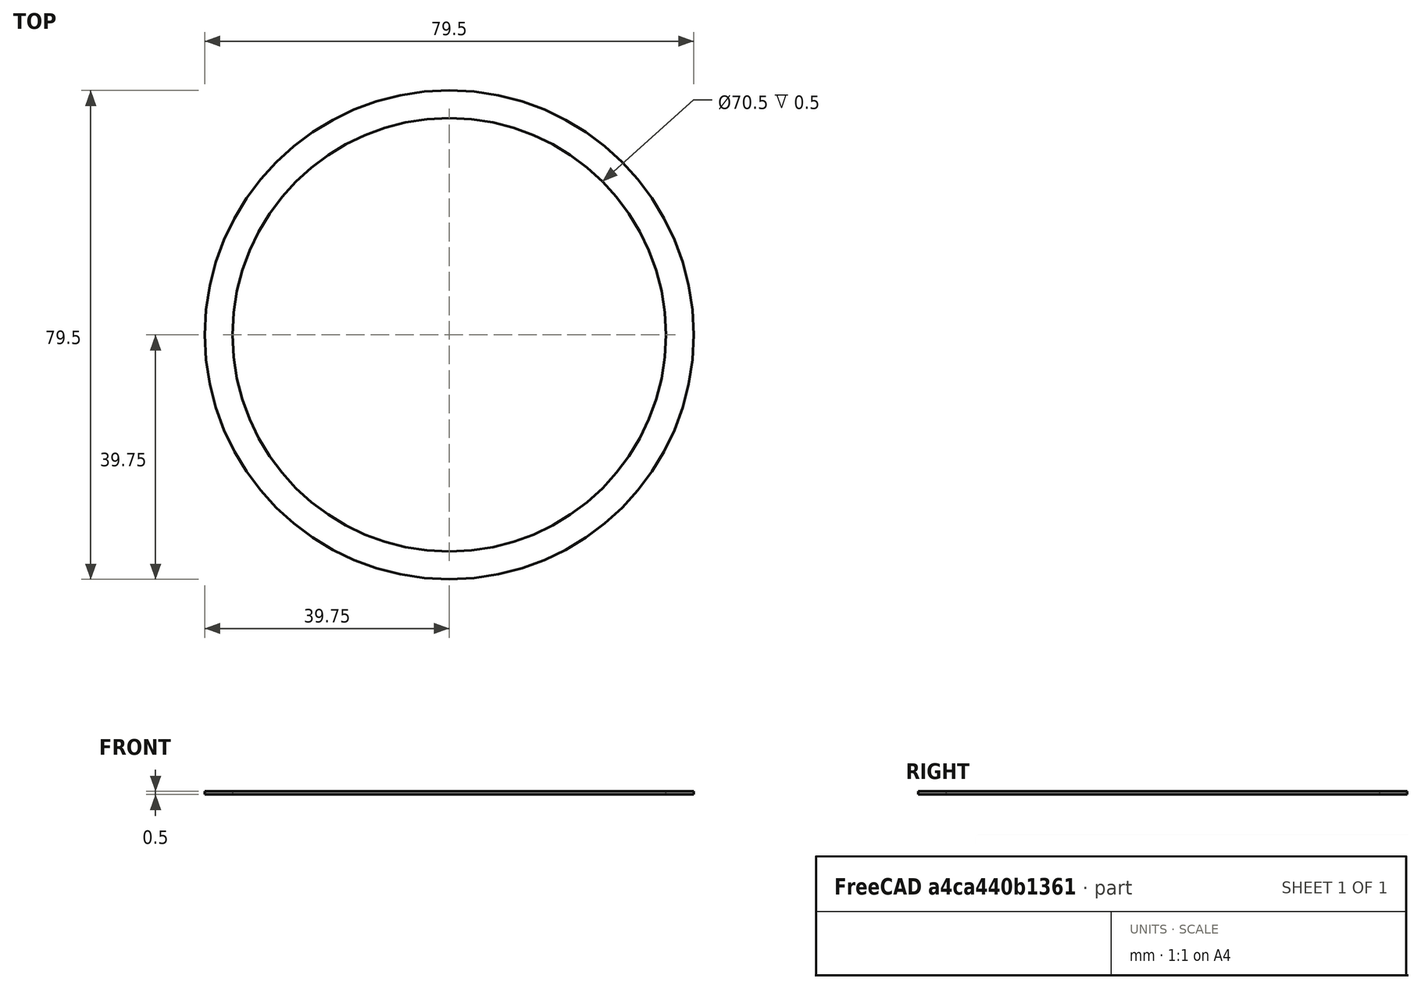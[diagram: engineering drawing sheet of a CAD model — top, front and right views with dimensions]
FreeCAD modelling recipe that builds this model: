
FCSTD DOCUMENT  (FreeCAD 0.19R24276 (Git))
Label: Ring_d79_5__d70_5
License: All rights reserved
LicenseURL: http://en.wikipedia.org/wiki/All_rights_reserved
objects: Sketcher::SketchObject×1, PartDesign::Pad×1, PartDesign::Body×1
note: 4 computed .brp shape members not serialized (recipe doc carries the construction recipe); baked Part::Feature solids carry a one-line shape summary decoded from their .brp

FEATURE [Sketcher::SketchObject] Sketch
  FullyConstrained = true
  MapMode = 5
  Support = -> [XY_Plane]
  sketch-geometry (2):
    g0: Circle CenterX=0 CenterY=0 CenterZ=0 NormalX=0 NormalY=0 NormalZ=1 AngleXU=0 Radius=39.75
    g1: Circle CenterX=0 CenterY=0 CenterZ=0 NormalX=0 NormalY=0 NormalZ=1 AngleXU=0 Radius=35.25
  constraints (4):
    c: Coincident(g0,g-1)
    c: Diameter(g0) = 79.5
    c: Coincident(g1,g0)
    c: Diameter(g1) = 70.5
FEATURE [PartDesign::Pad] Pad
  Direction = (1,1,1)
  Length = 0.5
  Length2 = 100
  Profile = -> Sketch
  Type = 0
FEATURE [PartDesign::Body] Body
  Group = -> [Sketch,Pad]
  Origin = -> Origin
  Tip = -> Pad
